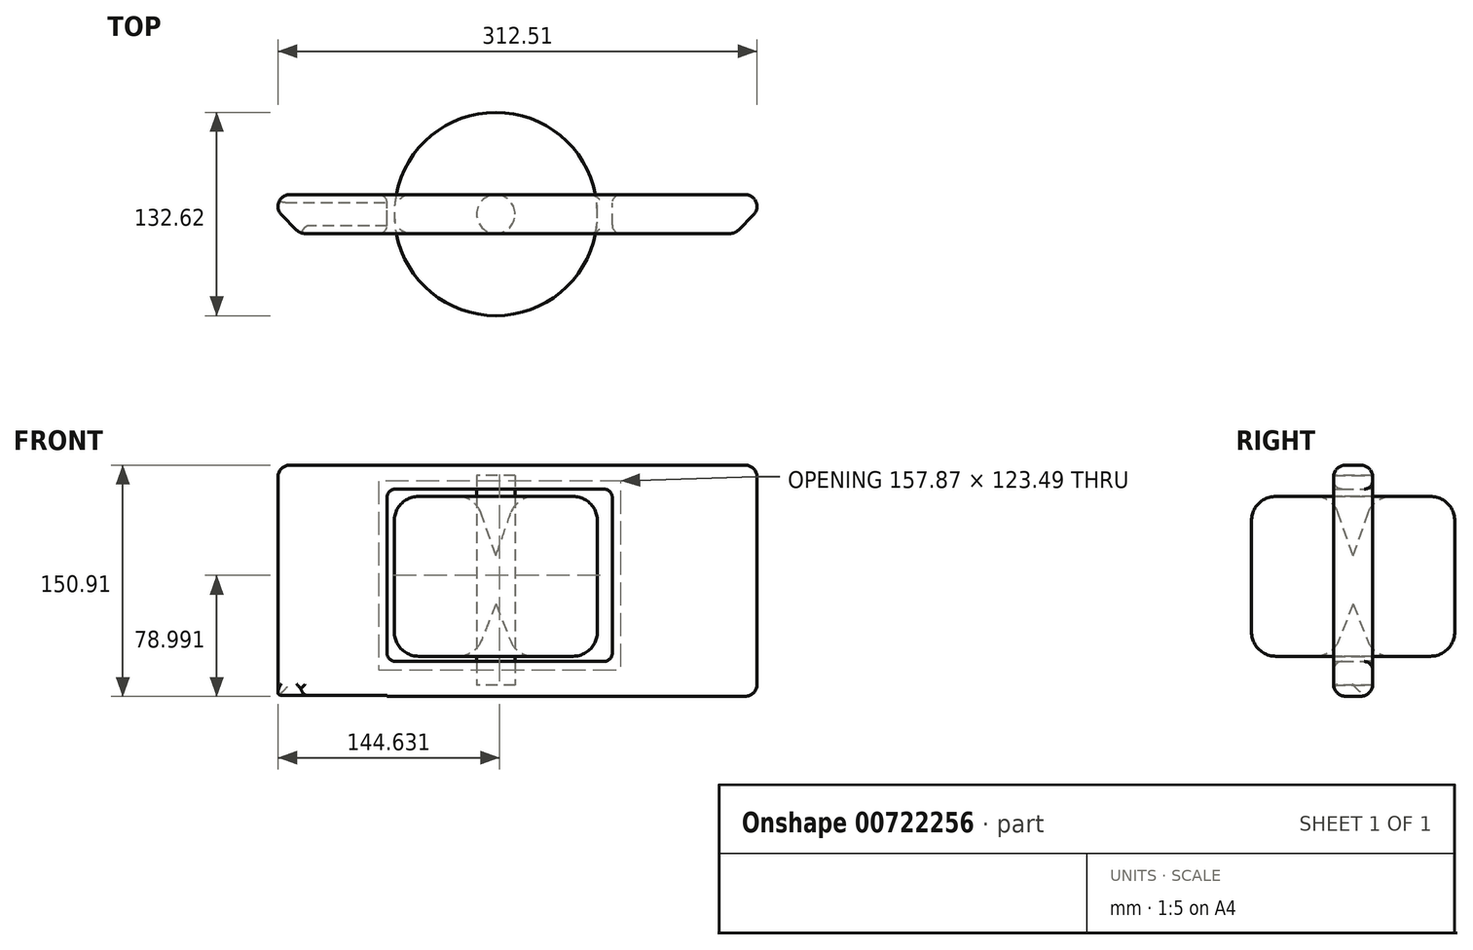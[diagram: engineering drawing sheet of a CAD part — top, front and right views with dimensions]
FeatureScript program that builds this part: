
annotation { "Feature Type Name" : "Feature", "Feature Type Description" : "" }
export const myFeature = defineFeature(function(context is Context, id is Id, definition is map)
    precondition{}
    {
        {
            var Q0;
            Q0=qCreatedBy(makeId("Front.planeOp"),FACE);
            var sketch = newSketch(context, id + "F0", { "sketchPlane" : qUnion([Q0])});
            skLineSegment(sketch, "E0.bottom", {"start": v(-13.54, 54.61) * mm, "end": v(-66.31, 54.61) * mm});
            skLineSegment(sketch, "E0.top", {"start": v(-13.54, -49.67) * mm, "end": v(-66.31, -49.67) * mm});
            skLineSegment(sketch, "E0.left", {"start": v(-13.54, 54.61) * mm, "end": v(-13.54, -49.67) * mm});
            skLineSegment(sketch, "E0.right", {"start": v(-66.31, 54.61) * mm, "end": v(-66.31, -49.67) * mm});
            skLineSegment(sketch, "E1", {"start": v(-13.54, 54.61) * mm, "end": v(0, 15.91) * mm});
            skLineSegment(sketch, "E2", {"start": v(0, 15.91) * mm, "end": v(0, -15.63) * mm});
            skLineSegment(sketch, "E3", {"start": v(0, -15.63) * mm, "end": v(-13.54, -49.67) * mm});
            skSolve(sketch);
        }
        {
            var Q0;
            Q0=makeQuery(id+"F0.imprint","IMPRINT",FACE,{"disambiguationData":[TD([[makeQuery(id+"F0.imprint","IMPRINT",EDGE,{"derivedFrom":sQuery(id+"F0.wireOp",EDGE,"E0.bottom")}),1.0]])]});
            var Q1;
            Q1=makeQuery(id+"F0.imprint","IMPRINT",FACE,{"disambiguationData":[TD([[makeQuery(id+"F0.imprint","IMPRINT",EDGE,{"derivedFrom":sQuery(id+"F0.wireOp",EDGE,"E0.left")}),1.0]])]});
            var Q2;
            Q2=sQuery(id+"F0.wireOp",EDGE,"E2");
            revolve(context, id + "F1", {"surfaceOperationType" : NewSurfaceOperationType.NEW, "entities" : qUnion([Q0, Q1]), "axis" : qUnion([Q2]), "revolveType" : RevolveType.FULL});
        }
        {
            var Q0;
            Q0=makeQuery(id+"F1.opRevolve","SWEPT_EDGE",EDGE,{"disambiguationData":[OSD([sQuery(id+"F0.wireOp",EDGE,"E0.bottom"),sQuery(id+"F0.wireOp",EDGE,"E0.left"),sQuery(id+"F0.wireOp",EDGE,"E1")])]});
            var Q1;
            Q1=makeQuery(id+"F1.opRevolve","SWEPT_EDGE",EDGE,{"disambiguationData":[OSD([sQuery(id+"F0.wireOp",EDGE,"E0.top"),sQuery(id+"F0.wireOp",EDGE,"E0.left"),sQuery(id+"F0.wireOp",EDGE,"E3")])]});
            var Q2;
            Q2=makeQuery(id+"F1.opRevolve","SWEPT_EDGE",EDGE,{"disambiguationData":[OSD([sQuery(id+"F0.wireOp",EDGE,"E0.top"),sQuery(id+"F0.wireOp",EDGE,"E0.right")])]});
            var Q3;
            Q3=makeQuery(id+"F1.opRevolve","SWEPT_EDGE",EDGE,{"disambiguationData":[OSD([sQuery(id+"F0.wireOp",EDGE,"E0.bottom"),sQuery(id+"F0.wireOp",EDGE,"E0.right")])]});
            fillet(context, id + "F2", {"entities" : qUnion([Q0, Q1, Q2, Q3]), "radius" : 15.93 * mm, "tangentPropagation" : true, "allowEdgeOverflow" : false});
        }
        {
            var Q0;
            Q0=qCreatedBy(makeId("Front.planeOp"),FACE);
            var sketch = newSketch(context, id + "F3", { "sketchPlane" : qUnion([Q0])});
            skLineSegment(sketch, "E4.bottom", {"start": v(-70.95, 75.1) * mm, "end": v(-178.52, 75.1) * mm});
            skLineSegment(sketch, "E4.top", {"start": v(-70.95, -75.31) * mm, "end": v(-178.52, -75.31) * mm});
            skLineSegment(sketch, "E4.left", {"start": v(-70.95, 75.1) * mm, "end": v(-70.95, -75.31) * mm});
            skLineSegment(sketch, "E4.right", {"start": v(-178.52, 75.1) * mm, "end": v(-178.52, -75.31) * mm});
            skLineSegment(sketch, "E5.bottom", {"start": v(-70.95, -53.1) * mm, "end": v(75.93, -53.1) * mm});
            skLineSegment(sketch, "E5.top", {"start": v(-70.95, -75.82) * mm, "end": v(75.93, -75.82) * mm});
            skLineSegment(sketch, "E5.left", {"start": v(-70.95, -53.1) * mm, "end": v(-70.95, -75.82) * mm});
            skLineSegment(sketch, "E5.right", {"start": v(75.93, -53.1) * mm, "end": v(75.93, -75.82) * mm});
            skLineSegment(sketch, "E6.bottom", {"start": v(75.93, -75.82) * mm, "end": v(206.76, -75.82) * mm});
            skLineSegment(sketch, "E6.top", {"start": v(75.93, 75.1) * mm, "end": v(206.76, 75.1) * mm});
            skLineSegment(sketch, "E6.left", {"start": v(75.93, -75.82) * mm, "end": v(75.93, 75.1) * mm});
            skLineSegment(sketch, "E6.right", {"start": v(206.76, -75.82) * mm, "end": v(206.76, 75.1) * mm});
            skLineSegment(sketch, "E7.bottom", {"start": v(75.93, 75.1) * mm, "end": v(-70.95, 75.1) * mm});
            skLineSegment(sketch, "E7.top", {"start": v(75.93, 59.45) * mm, "end": v(-70.95, 59.45) * mm});
            skLineSegment(sketch, "E7.left", {"start": v(75.93, 75.1) * mm, "end": v(75.93, 59.45) * mm});
            skLineSegment(sketch, "E7.right", {"start": v(-70.95, 75.1) * mm, "end": v(-70.95, 59.45) * mm});
            skSolve(sketch);
        }
        {
            var Q0;
            Q0 = qSketchRegion(id + "F3", true);
            extrude(context, id + "F4", {"entities" : qUnion([Q0]), "endBound" : BoundingType.SYMMETRIC, "depth" : 25.4 * mm, "offsetDistance" : 25.4 * mm});
        }
        {
            var Q0;
            Q0=qCreatedBy(makeId("Top.planeOp"),FACE);
            var sketch = newSketch(context, id + "F5", { "sketchPlane" : qUnion([Q0])});
            skCircle(sketch, "E8", {"center": v(0, 0) * mm, "radius": 12.6 * mm});
            skSolve(sketch);
        }
        {
            var Q0;
            Q0 = qSketchRegion(id + "F5", true);
            extrude(context, id + "F6", {"entities" : qUnion([Q0]), "endBound" : BoundingType.SYMMETRIC, "depth" : 136.88 * mm, "offsetDistance" : 25.4 * mm});
        }
        {
            var Q0;
            Q0=makeQuery(id+"F4.opExtrude","CAP_EDGE",EDGE,{"disambiguationData":[OSD([sQuery(id+"F3.wireOp",EDGE,"E4.right")])],"isStart":false});
            var Q1;
            Q1=makeQuery(id+"F4.opExtrude","CAP_EDGE",EDGE,{"disambiguationData":[OSD([sQuery(id+"F3.wireOp",EDGE,"E6.right")])],"isStart":false});
            chamfer(context, id + "F7", {"entities" : qUnion([Q0, Q1]), "width" : 50.8 * mm, "tangentPropagation" : true});
        }
        {
            var Q0;
            Q0=makeQuery(id+"F4.opExtrude","CAP_EDGE",EDGE,{"disambiguationData":[OSD([sQuery(id+"F3.wireOp",EDGE,"E4.bottom"),sQuery(id+"F3.wireOp",EDGE,"E6.top"),sQuery(id+"F3.wireOp",EDGE,"E7.bottom")])],"isStart":true});
            var Q1;
            Q1=makeQuery(id+"F4.opExtrude","CAP_EDGE",EDGE,{"disambiguationData":[OSD([sQuery(id+"F3.wireOp",EDGE,"E4.bottom"),sQuery(id+"F3.wireOp",EDGE,"E6.top"),sQuery(id+"F3.wireOp",EDGE,"E7.bottom")])],"isStart":false});
            var Q2;
            Q2=makeQuery(id+"F4.opExtrude","CAP_EDGE",EDGE,{"disambiguationData":[OSD([sQuery(id+"F3.wireOp",EDGE,"E5.top"),sQuery(id+"F3.wireOp",EDGE,"E6.bottom")])],"isStart":false});
            var Q3;
            Q3=makeQuery(id+"F4.opExtrude","CAP_EDGE",EDGE,{"disambiguationData":[OSD([sQuery(id+"F3.wireOp",EDGE,"E5.top"),sQuery(id+"F3.wireOp",EDGE,"E6.bottom")])],"isStart":true});
            var Q4;
            {var subQ0=sQuery(id+"F3.wireOp",EDGE,"E4.right");Q4=makeQuery(id+"F7.opChamfer","BLEND_EDGE",EDGE,{"blendedFrom":[makeQuery(id+"F4.opExtrude","CAP_EDGE",EDGE,{"disambiguationData":[OSD([subQ0])],"isStart":false}),makeQuery(id+"F4.opExtrude","CAP_FACE",FACE,{"disambiguationData":[OSD([sQuery(id+"F3.wireOp",EDGE,"E4.bottom"),sQuery(id+"F3.wireOp",EDGE,"E4.top"),sQuery(id+"F3.wireOp",EDGE,"E4.left"),subQ0,sQuery(id+"F3.wireOp",EDGE,"E5.bottom"),sQuery(id+"F3.wireOp",EDGE,"E5.top"),sQuery(id+"F3.wireOp",EDGE,"E5.left"),sQuery(id+"F3.wireOp",EDGE,"E6.bottom"),sQuery(id+"F3.wireOp",EDGE,"E6.top"),sQuery(id+"F3.wireOp",EDGE,"E6.left"),sQuery(id+"F3.wireOp",EDGE,"E6.right"),sQuery(id+"F3.wireOp",EDGE,"E7.bottom"),sQuery(id+"F3.wireOp",EDGE,"E7.top")])],"isStart":true})],"blendedInto":[makeQuery(id+"F4.opExtrude","CAP_FACE",FACE,{"disambiguationData":[OSD([sQuery(id+"F3.wireOp",EDGE,"E4.bottom"),sQuery(id+"F3.wireOp",EDGE,"E4.top"),sQuery(id+"F3.wireOp",EDGE,"E4.left"),subQ0,sQuery(id+"F3.wireOp",EDGE,"E5.bottom"),sQuery(id+"F3.wireOp",EDGE,"E5.top"),sQuery(id+"F3.wireOp",EDGE,"E5.left"),sQuery(id+"F3.wireOp",EDGE,"E6.bottom"),sQuery(id+"F3.wireOp",EDGE,"E6.top"),sQuery(id+"F3.wireOp",EDGE,"E6.left"),sQuery(id+"F3.wireOp",EDGE,"E6.right"),sQuery(id+"F3.wireOp",EDGE,"E7.bottom"),sQuery(id+"F3.wireOp",EDGE,"E7.top")])],"isStart":true})]});}
            var Q5;
            {var subQ0=sQuery(id+"F3.wireOp",EDGE,"E4.right");Q5=makeQuery(id+"F7.opChamfer","BLEND_EDGE",EDGE,{"blendedFrom":[makeQuery(id+"F4.opExtrude","CAP_EDGE",EDGE,{"disambiguationData":[OSD([subQ0])],"isStart":false}),makeQuery(id+"F4.opExtrude","CAP_FACE",FACE,{"disambiguationData":[OSD([sQuery(id+"F3.wireOp",EDGE,"E4.bottom"),sQuery(id+"F3.wireOp",EDGE,"E4.top"),sQuery(id+"F3.wireOp",EDGE,"E4.left"),subQ0,sQuery(id+"F3.wireOp",EDGE,"E5.bottom"),sQuery(id+"F3.wireOp",EDGE,"E5.top"),sQuery(id+"F3.wireOp",EDGE,"E5.left"),sQuery(id+"F3.wireOp",EDGE,"E6.bottom"),sQuery(id+"F3.wireOp",EDGE,"E6.top"),sQuery(id+"F3.wireOp",EDGE,"E6.left"),sQuery(id+"F3.wireOp",EDGE,"E6.right"),sQuery(id+"F3.wireOp",EDGE,"E7.bottom"),sQuery(id+"F3.wireOp",EDGE,"E7.top")])],"isStart":false})],"blendedInto":[makeQuery(id+"F4.opExtrude","CAP_FACE",FACE,{"disambiguationData":[OSD([sQuery(id+"F3.wireOp",EDGE,"E4.bottom"),sQuery(id+"F3.wireOp",EDGE,"E4.top"),sQuery(id+"F3.wireOp",EDGE,"E4.left"),subQ0,sQuery(id+"F3.wireOp",EDGE,"E5.bottom"),sQuery(id+"F3.wireOp",EDGE,"E5.top"),sQuery(id+"F3.wireOp",EDGE,"E5.left"),sQuery(id+"F3.wireOp",EDGE,"E6.bottom"),sQuery(id+"F3.wireOp",EDGE,"E6.top"),sQuery(id+"F3.wireOp",EDGE,"E6.left"),sQuery(id+"F3.wireOp",EDGE,"E6.right"),sQuery(id+"F3.wireOp",EDGE,"E7.bottom"),sQuery(id+"F3.wireOp",EDGE,"E7.top")])],"isStart":false})]});}
            var Q6;
            Q6=makeQuery(id+"F7.opChamfer","BLEND_EDGE",EDGE,{"blendedFrom":[makeQuery(id+"F4.opExtrude","CAP_EDGE",EDGE,{"disambiguationData":[OSD([sQuery(id+"F3.wireOp",EDGE,"E4.right")])],"isStart":false}),makeQuery(id+"F4.opExtrude","SWEPT_FACE",FACE,{"disambiguationData":[OSD([sQuery(id+"F3.wireOp",EDGE,"E4.top")])]})],"blendedInto":[makeQuery(id+"F4.opExtrude","SWEPT_FACE",FACE,{"disambiguationData":[OSD([sQuery(id+"F3.wireOp",EDGE,"E4.top")])]})]});
            var Q7;
            Q7=makeQuery(id+"F7.opChamfer","BLEND_EDGE",EDGE,{"blendedFrom":[makeQuery(id+"F4.opExtrude","CAP_EDGE",EDGE,{"disambiguationData":[OSD([sQuery(id+"F3.wireOp",EDGE,"E4.right")])],"isStart":false}),makeQuery(id+"F4.opExtrude","SWEPT_FACE",FACE,{"disambiguationData":[OSD([sQuery(id+"F3.wireOp",EDGE,"E4.bottom"),sQuery(id+"F3.wireOp",EDGE,"E6.top"),sQuery(id+"F3.wireOp",EDGE,"E7.bottom")])]})],"blendedInto":[makeQuery(id+"F4.opExtrude","SWEPT_FACE",FACE,{"disambiguationData":[OSD([sQuery(id+"F3.wireOp",EDGE,"E4.bottom"),sQuery(id+"F3.wireOp",EDGE,"E6.top"),sQuery(id+"F3.wireOp",EDGE,"E7.bottom")])]})]});
            var Q8;
            {var subQ0=sQuery(id+"F3.wireOp",EDGE,"E6.right");Q8=makeQuery(id+"F7.opChamfer","BLEND_EDGE",EDGE,{"blendedFrom":[makeQuery(id+"F4.opExtrude","CAP_EDGE",EDGE,{"disambiguationData":[OSD([subQ0])],"isStart":false}),makeQuery(id+"F4.opExtrude","CAP_FACE",FACE,{"disambiguationData":[OSD([sQuery(id+"F3.wireOp",EDGE,"E4.bottom"),sQuery(id+"F3.wireOp",EDGE,"E4.top"),sQuery(id+"F3.wireOp",EDGE,"E4.left"),sQuery(id+"F3.wireOp",EDGE,"E4.right"),sQuery(id+"F3.wireOp",EDGE,"E5.bottom"),sQuery(id+"F3.wireOp",EDGE,"E5.top"),sQuery(id+"F3.wireOp",EDGE,"E5.left"),sQuery(id+"F3.wireOp",EDGE,"E6.bottom"),sQuery(id+"F3.wireOp",EDGE,"E6.top"),sQuery(id+"F3.wireOp",EDGE,"E6.left"),subQ0,sQuery(id+"F3.wireOp",EDGE,"E7.bottom"),sQuery(id+"F3.wireOp",EDGE,"E7.top")])],"isStart":true})],"blendedInto":[makeQuery(id+"F4.opExtrude","CAP_FACE",FACE,{"disambiguationData":[OSD([sQuery(id+"F3.wireOp",EDGE,"E4.bottom"),sQuery(id+"F3.wireOp",EDGE,"E4.top"),sQuery(id+"F3.wireOp",EDGE,"E4.left"),sQuery(id+"F3.wireOp",EDGE,"E4.right"),sQuery(id+"F3.wireOp",EDGE,"E5.bottom"),sQuery(id+"F3.wireOp",EDGE,"E5.top"),sQuery(id+"F3.wireOp",EDGE,"E5.left"),sQuery(id+"F3.wireOp",EDGE,"E6.bottom"),sQuery(id+"F3.wireOp",EDGE,"E6.top"),sQuery(id+"F3.wireOp",EDGE,"E6.left"),subQ0,sQuery(id+"F3.wireOp",EDGE,"E7.bottom"),sQuery(id+"F3.wireOp",EDGE,"E7.top")])],"isStart":true})]});}
            var Q9;
            {var subQ0=sQuery(id+"F3.wireOp",EDGE,"E6.right");Q9=makeQuery(id+"F7.opChamfer","BLEND_EDGE",EDGE,{"blendedFrom":[makeQuery(id+"F4.opExtrude","CAP_EDGE",EDGE,{"disambiguationData":[OSD([subQ0])],"isStart":false}),makeQuery(id+"F4.opExtrude","CAP_FACE",FACE,{"disambiguationData":[OSD([sQuery(id+"F3.wireOp",EDGE,"E4.bottom"),sQuery(id+"F3.wireOp",EDGE,"E4.top"),sQuery(id+"F3.wireOp",EDGE,"E4.left"),sQuery(id+"F3.wireOp",EDGE,"E4.right"),sQuery(id+"F3.wireOp",EDGE,"E5.bottom"),sQuery(id+"F3.wireOp",EDGE,"E5.top"),sQuery(id+"F3.wireOp",EDGE,"E5.left"),sQuery(id+"F3.wireOp",EDGE,"E6.bottom"),sQuery(id+"F3.wireOp",EDGE,"E6.top"),sQuery(id+"F3.wireOp",EDGE,"E6.left"),subQ0,sQuery(id+"F3.wireOp",EDGE,"E7.bottom"),sQuery(id+"F3.wireOp",EDGE,"E7.top")])],"isStart":false})],"blendedInto":[makeQuery(id+"F4.opExtrude","CAP_FACE",FACE,{"disambiguationData":[OSD([sQuery(id+"F3.wireOp",EDGE,"E4.bottom"),sQuery(id+"F3.wireOp",EDGE,"E4.top"),sQuery(id+"F3.wireOp",EDGE,"E4.left"),sQuery(id+"F3.wireOp",EDGE,"E4.right"),sQuery(id+"F3.wireOp",EDGE,"E5.bottom"),sQuery(id+"F3.wireOp",EDGE,"E5.top"),sQuery(id+"F3.wireOp",EDGE,"E5.left"),sQuery(id+"F3.wireOp",EDGE,"E6.bottom"),sQuery(id+"F3.wireOp",EDGE,"E6.top"),sQuery(id+"F3.wireOp",EDGE,"E6.left"),subQ0,sQuery(id+"F3.wireOp",EDGE,"E7.bottom"),sQuery(id+"F3.wireOp",EDGE,"E7.top")])],"isStart":false})]});}
            var Q10;
            Q10=makeQuery(id+"F7.opChamfer","BLEND_EDGE",EDGE,{"blendedFrom":[makeQuery(id+"F4.opExtrude","CAP_EDGE",EDGE,{"disambiguationData":[OSD([sQuery(id+"F3.wireOp",EDGE,"E6.right")])],"isStart":false}),makeQuery(id+"F4.opExtrude","SWEPT_FACE",FACE,{"disambiguationData":[OSD([sQuery(id+"F3.wireOp",EDGE,"E5.top"),sQuery(id+"F3.wireOp",EDGE,"E6.bottom")])]})],"blendedInto":[makeQuery(id+"F4.opExtrude","SWEPT_FACE",FACE,{"disambiguationData":[OSD([sQuery(id+"F3.wireOp",EDGE,"E5.top"),sQuery(id+"F3.wireOp",EDGE,"E6.bottom")])]})]});
            var Q11;
            Q11=makeQuery(id+"F7.opChamfer","BLEND_EDGE",EDGE,{"blendedFrom":[makeQuery(id+"F4.opExtrude","CAP_EDGE",EDGE,{"disambiguationData":[OSD([sQuery(id+"F3.wireOp",EDGE,"E6.right")])],"isStart":false}),makeQuery(id+"F4.opExtrude","SWEPT_FACE",FACE,{"disambiguationData":[OSD([sQuery(id+"F3.wireOp",EDGE,"E4.bottom"),sQuery(id+"F3.wireOp",EDGE,"E6.top"),sQuery(id+"F3.wireOp",EDGE,"E7.bottom")])]})],"blendedInto":[makeQuery(id+"F4.opExtrude","SWEPT_FACE",FACE,{"disambiguationData":[OSD([sQuery(id+"F3.wireOp",EDGE,"E4.bottom"),sQuery(id+"F3.wireOp",EDGE,"E6.top"),sQuery(id+"F3.wireOp",EDGE,"E7.bottom")])]})]});
            fillet(context, id + "F8", {"entities" : qUnion([Q0, Q1, Q2, Q3, Q4, Q5, Q6, Q7, Q8, Q9, Q10, Q11]), "radius" : 7.77 * mm, "tangentPropagation" : true, "allowEdgeOverflow" : false});
        }
        {
            var Q0;
            Q0=makeQuery(id+"F4.opExtrude","SWEPT_FACE",FACE,{"disambiguationData":[OSD([sQuery(id+"F3.wireOp",EDGE,"E4.left")])]});
            var Q1;
            Q1=makeQuery(id+"F4.opExtrude","SWEPT_FACE",FACE,{"disambiguationData":[OSD([sQuery(id+"F3.wireOp",EDGE,"E6.left")])]});
            fillet(context, id + "F9", {"entities" : qUnion([Q0, Q1]), "radius" : 5.5 * mm, "tangentPropagation" : true, "allowEdgeOverflow" : false});
        }
    });
